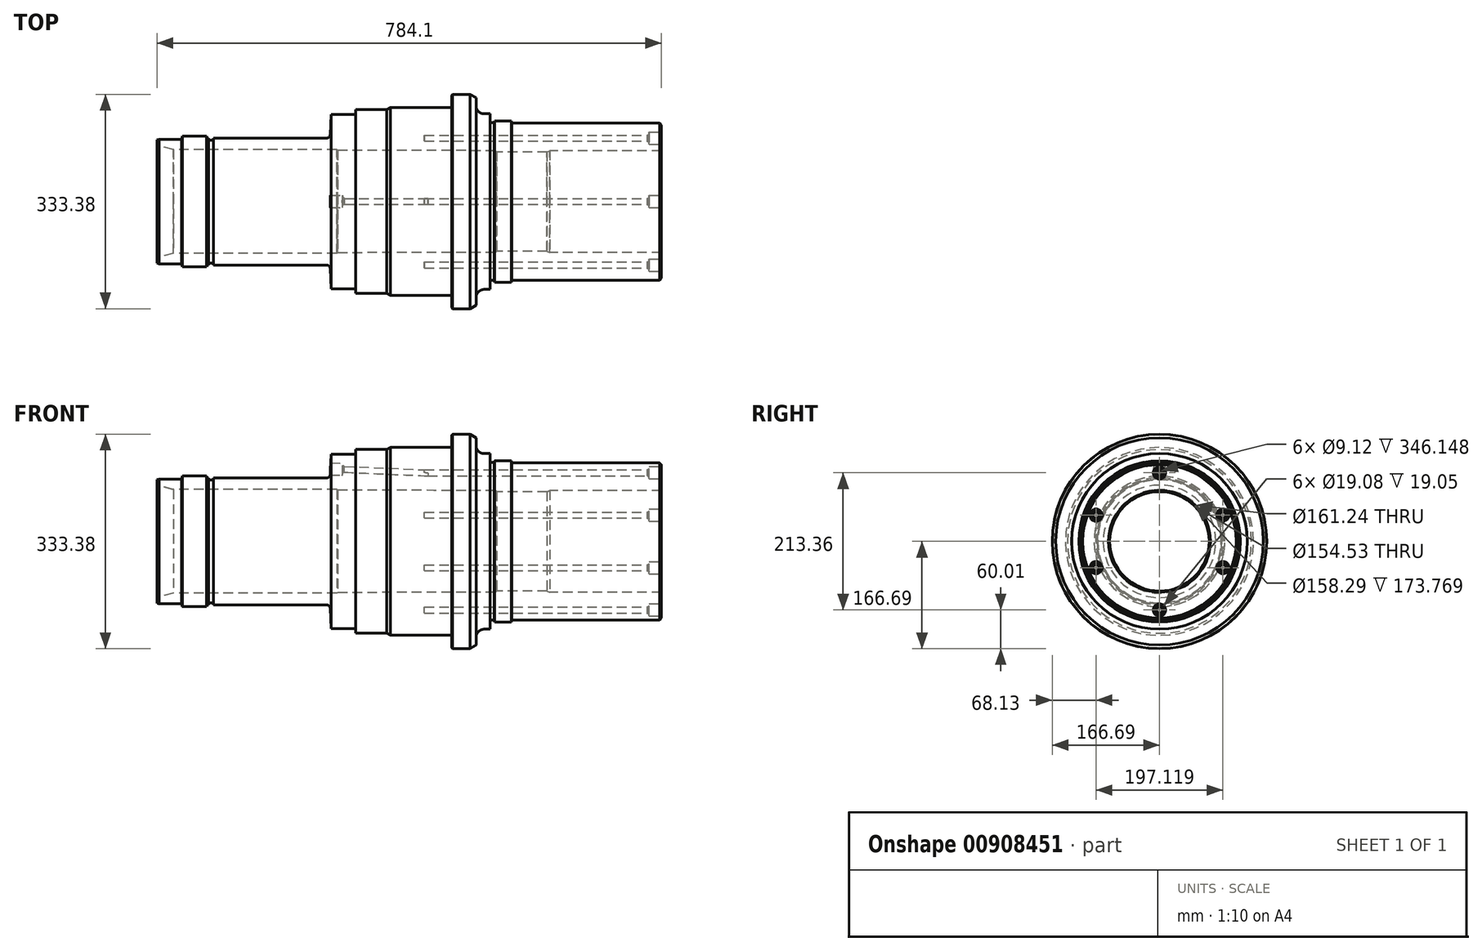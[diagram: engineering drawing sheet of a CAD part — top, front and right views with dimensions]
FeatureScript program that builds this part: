
annotation { "Feature Type Name" : "Feature", "Feature Type Description" : "" }
export const myFeature = defineFeature(function(context is Context, id is Id, definition is map)
    precondition{}
    {
        {
            var Q0;
            Q0=qCreatedBy(makeId("Front.planeOp"),FACE);
            var sketch = newSketch(context, id + "F0", { "sketchPlane" : qUnion([Q0])});
            skLineSegment(sketch, "E0", {"start": v(0, 0) * mm, "end": v(784.1, 0) * mm, "construction": true});
            skLineSegment(sketch, "E1", {"start": v(0, 96.84) * mm, "end": v(38.1, 96.84) * mm});
            skLineSegment(sketch, "E2", {"start": v(25.55, 80.62) * mm, "end": v(279.4, 80.62) * mm});
            skLineSegment(sketch, "E3", {"start": v(39.38, 101.6) * mm, "end": v(77, 101.6) * mm});
            skLineSegment(sketch, "E4", {"start": v(77.72, 98.87) * mm, "end": v(80.16, 98.87) * mm});
            skLineSegment(sketch, "E5", {"start": v(80.16, 98.87) * mm, "end": v(80.16, 95.7) * mm});
            skLineSegment(sketch, "E6", {"start": v(80.16, 95.7) * mm, "end": v(88.09, 95.7) * mm});
            skLineSegment(sketch, "E7", {"start": v(88.09, 95.7) * mm, "end": v(88.09, 98.87) * mm});
            skLineSegment(sketch, "E8", {"start": v(88.09, 98.87) * mm, "end": v(268.98, 98.87) * mm});
            skLineSegment(sketch, "E9", {"start": v(270.59, 135.64) * mm, "end": v(308.69, 135.64) * mm});
            skLineSegment(sketch, "E10", {"start": v(308.69, 135.64) * mm, "end": v(308.69, 142.88) * mm});
            skLineSegment(sketch, "E11", {"start": v(308.69, 142.88) * mm, "end": v(357.2, 142.88) * mm});
            skLineSegment(sketch, "E12", {"start": v(357.2, 142.87) * mm, "end": v(362.7, 146.05) * mm});
            skLineSegment(sketch, "E13", {"start": v(362.7, 146.05) * mm, "end": v(457.99, 146.05) * mm});
            skLineSegment(sketch, "E14", {"start": v(457.99, 146.05) * mm, "end": v(457.99, 166.69) * mm});
            skLineSegment(sketch, "E15", {"start": v(457.99, 166.69) * mm, "end": v(495.94, 166.69) * mm});
            skLineSegment(sketch, "E16", {"start": v(495.94, 166.69) * mm, "end": v(495.94, 136.53) * mm});
            skLineSegment(sketch, "E17", {"start": v(495.94, 136.53) * mm, "end": v(517.52, 136.53) * mm});
            skLineSegment(sketch, "E18", {"start": v(517.52, 136.53) * mm, "end": v(517.52, 122.5) * mm});
            skLineSegment(sketch, "E19", {"start": v(517.52, 122.5) * mm, "end": v(523.88, 122.5) * mm});
            skLineSegment(sketch, "E20", {"start": v(523.88, 122.5) * mm, "end": v(524.65, 125.41) * mm});
            skLineSegment(sketch, "E21", {"start": v(524.65, 125.41) * mm, "end": v(550.85, 125.41) * mm});
            skLineSegment(sketch, "E22", {"start": v(550.85, 125.41) * mm, "end": v(551.7, 122.24) * mm});
            skLineSegment(sketch, "E23", {"start": v(551.7, 122.24) * mm, "end": v(784.1, 122.24) * mm});
            skLineSegment(sketch, "E24", {"start": v(784.1, 79.15) * mm, "end": v(784.1, 122.24) * mm});
            skLineSegment(sketch, "E25", {"start": v(784.1, 79.15) * mm, "end": v(610.33, 79.15) * mm});
            skLineSegment(sketch, "E26", {"start": v(610.33, 79.15) * mm, "end": v(606.3, 77.27) * mm});
            skLineSegment(sketch, "E27", {"start": v(606.3, 77.27) * mm, "end": v(527.92, 77.27) * mm});
            skLineSegment(sketch, "E28", {"start": v(279.4, 80.62) * mm, "end": v(281.23, 79.57) * mm});
            skLineSegment(sketch, "E29", {"start": v(281.23, 79.57) * mm, "end": v(526.04, 79.15) * mm});
            skLineSegment(sketch, "E30", {"start": v(527.92, 77.27) * mm, "end": v(526.04, 79.15) * mm});
            skLineSegment(sketch, "E31", {"start": v(268.98, 98.87) * mm, "end": v(270.59, 135.64) * mm});
            skLineSegment(sketch, "E32", {"start": v(38.1, 96.84) * mm, "end": v(39.38, 101.6) * mm});
            skLineSegment(sketch, "E33", {"start": v(77.72, 98.87) * mm, "end": v(77, 101.6) * mm});
            skPoint(sketch, "E34.end.orphan", {"position": v(38.1, 101.6) * mm});
            skLineSegment(sketch, "E35", {"start": v(0, 87.46) * mm, "end": v(25.55, 80.62) * mm});
            skLineSegment(sketch, "E36", {"start": v(0, 96.84) * mm, "end": v(0, 87.46) * mm});
            skSolve(sketch);
        }
        {
            var Q0;
            Q0=qSketchRegion(id+"F0",true);
            var Q1;
            Q1=sQuery(id+"F0.wireOp",EDGE,"E0");
            revolve(context, id + "F1", {"surfaceOperationType" : NewSurfaceOperationType.NEW, "entities" : qUnion([Q0]), "axis" : qUnion([Q1]), "revolveType" : RevolveType.FULL});
        }
        {
            var Q0;
            Q0=makeQuery(id+"F1.opRevolve","SWEPT_EDGE",EDGE,{"disambiguationData":[OSD([sQuery(id+"F0.wireOp",EDGE,"E15"),sQuery(id+"F0.wireOp",EDGE,"E16")])]});
            chamfer(context, id + "F2", {"entities" : qUnion([Q0]), "chamferType" : ChamferType.OFFSET_ANGLE, "width" : 9.52 * mm, "oppositeDirection" : false, "angle" : 30 * degree, "tangentPropagation" : true});
        }
        {
            var Q0;
            Q0=makeQuery(id+"F1.opRevolve","SWEPT_EDGE",EDGE,{"disambiguationData":[OSD([sQuery(id+"F0.wireOp",EDGE,"E16"),sQuery(id+"F0.wireOp",EDGE,"E17")])]});
            fillet(context, id + "F3", {"entities" : qUnion([Q0]), "radius" : 12.7 * mm, "tangentPropagation" : true, "allowEdgeOverflow" : false});
        }
        {
            var Q0;
            Q0=makeQuery(id+"F1.opRevolve","SWEPT_EDGE",EDGE,{"disambiguationData":[OSD([sQuery(id+"F0.wireOp",EDGE,"E8"),sQuery(id+"F0.wireOp",EDGE,"E31")])]});
            fillet(context, id + "F4", {"entities" : qUnion([Q0]), "radius" : 5.08 * mm, "tangentPropagation" : true, "allowEdgeOverflow" : false});
        }
        {
            var Q0;
            Q0=makeQuery(id+"F1.opRevolve","SWEPT_EDGE",EDGE,{"disambiguationData":[OSD([sQuery(id+"F0.wireOp",EDGE,"E1"),sQuery(id+"F0.wireOp",EDGE,"SCYpA8kQ-7sTV-xUNJ-m1pp-K6qHX3d4gstn")])]});
            chamfer(context, id + "F5", {"entities" : qUnion([Q0]), "chamferType" : ChamferType.OFFSET_ANGLE, "width" : 0.86 * mm, "oppositeDirection" : false, "angle" : 75 * degree, "tangentPropagation" : true});
        }
        {
            var Q0;
            Q0=makeQuery(id+"F1.opRevolve","SWEPT_EDGE",EDGE,{"disambiguationData":[OSD([sQuery(id+"F0.wireOp",EDGE,"E23"),sQuery(id+"F0.wireOp",EDGE,"E24")])]});
            chamfer(context, id + "F6", {"entities" : qUnion([Q0]), "width" : 3.05 * mm, "tangentPropagation" : true});
        }
        {
            var Q0;
            Q0=makeQuery(id+"F1.opRevolve","SWEPT_EDGE",EDGE,{"disambiguationData":[OSD([sQuery(id+"F0.wireOp",EDGE,"E14"),sQuery(id+"F0.wireOp",EDGE,"E15")])]});
            chamfer(context, id + "F7", {"entities" : qUnion([Q0]), "width" : 1.52 * mm, "tangentPropagation" : true});
        }
        {
            var Q0;
            Q0=makeQuery(id+"F1.opRevolve","SWEPT_FACE",FACE,{"disambiguationData":[OSD([sQuery(id+"F0.wireOp",EDGE,"E24")])]});
            var sketch = newSketch(context, id + "F8", { "sketchPlane" : qUnion([Q0])});
            skCircle(sketch, "E37", {"center": v(0, 106.68) * mm, "radius": 4.56 * mm});
            skCircle(sketch, "E38", {"center": v(0, -106.68) * mm, "radius": 4.56 * mm});
            skCircle(sketch, "E39", {"center": v(98.52, 40.92) * mm, "radius": 4.56 * mm});
            skCircle(sketch, "E40", {"center": v(98.56, -40.82) * mm, "radius": 4.56 * mm});
            skCircle(sketch, "E41", {"center": v(-98.56, -40.82) * mm, "radius": 4.56 * mm});
            skCircle(sketch, "E42", {"center": v(-98.56, 40.83) * mm, "radius": 4.56 * mm});
            skLineSegment(sketch, "E43", {"start": v(-107.72, 0) * mm, "end": v(113.39, 0) * mm, "construction": true});
            skLineSegment(sketch, "E44", {"start": v(0, 0) * mm, "end": v(98.52, 40.92) * mm, "construction": true});
            skLineSegment(sketch, "E45", {"start": v(0, 0) * mm, "end": v(-98.56, 40.83) * mm, "construction": true});
            skLineSegment(sketch, "E46", {"start": v(0, 0) * mm, "end": v(-98.56, -40.82) * mm, "construction": true});
            skLineSegment(sketch, "E47", {"start": v(0, 0) * mm, "end": v(98.56, -40.82) * mm, "construction": true});
            skSolve(sketch);
        }
        {
            var Q0;
            Q0=qSketchRegion(id+"F8",true);
            extrude(context, id + "F9", {"entities" : qUnion([Q0]), "operationType" : NewBodyOperationType.REMOVE, "oppositeDirection" : true, "depth" : 368.3 * mm, "offsetDistance" : 25.4 * mm});
        }
        {
            var Q0;
            Q0=makeQuery(id+"F1.opRevolve","SWEPT_FACE",FACE,{"disambiguationData":[OSD([sQuery(id+"F0.wireOp",EDGE,"E24")])]});
            var sketch = newSketch(context, id + "F10", { "sketchPlane" : qUnion([Q0])});
            skCircle(sketch, "E48", {"center": v(98.52, 40.92) * mm, "radius": 9.54 * mm});
            skCircle(sketch, "E49", {"center": v(0, 106.68) * mm, "radius": 9.54 * mm});
            skCircle(sketch, "E50", {"center": v(-98.56, 40.83) * mm, "radius": 9.54 * mm});
            skCircle(sketch, "E51", {"center": v(-98.56, -40.82) * mm, "radius": 9.54 * mm});
            skCircle(sketch, "E52", {"center": v(98.56, -40.82) * mm, "radius": 9.54 * mm});
            skCircle(sketch, "E53", {"center": v(0, -106.68) * mm, "radius": 9.54 * mm});
            skSolve(sketch);
        }
        {
            var Q0;
            Q0=qSketchRegion(id+"F10",true);
            extrude(context, id + "F11", {"entities" : qUnion([Q0]), "operationType" : NewBodyOperationType.REMOVE, "oppositeDirection" : true, "depth" : 19.05 * mm, "offsetDistance" : 25.4 * mm});
        }
        {
            var Q0;
            Q0=makeQuery(id+"F11.boolean.opBoolean","INTERSECT",EDGE,{"derivedFrom":[makeQuery(id+"F9.boolean.opBoolean","COPY",FACE,{"derivedFrom":makeQuery(id+"F9.opExtrude","SWEPT_FACE",FACE,{"disambiguationData":[OSD([sQuery(id+"F8.wireOp",EDGE,"E37")])]})}),makeQuery(id+"F11.opExtrude","CAP_FACE",FACE,{"disambiguationData":[OSD([sQuery(id+"F10.wireOp",EDGE,"E49")])],"isStart":false})]});
            var Q1;
            Q1=makeQuery(id+"F11.boolean.opBoolean","INTERSECT",EDGE,{"derivedFrom":[makeQuery(id+"F9.boolean.opBoolean","COPY",FACE,{"derivedFrom":makeQuery(id+"F9.opExtrude","SWEPT_FACE",FACE,{"disambiguationData":[OSD([sQuery(id+"F8.wireOp",EDGE,"E42")])]})}),makeQuery(id+"F11.opExtrude","CAP_FACE",FACE,{"disambiguationData":[OSD([sQuery(id+"F10.wireOp",EDGE,"E50")])],"isStart":false})]});
            var Q2;
            Q2=makeQuery(id+"F11.boolean.opBoolean","INTERSECT",EDGE,{"derivedFrom":[makeQuery(id+"F9.boolean.opBoolean","COPY",FACE,{"derivedFrom":makeQuery(id+"F9.opExtrude","SWEPT_FACE",FACE,{"disambiguationData":[OSD([sQuery(id+"F8.wireOp",EDGE,"E38")])]})}),makeQuery(id+"F11.opExtrude","CAP_FACE",FACE,{"disambiguationData":[OSD([sQuery(id+"F10.wireOp",EDGE,"E53")])],"isStart":false})]});
            var Q3;
            Q3=makeQuery(id+"F11.boolean.opBoolean","INTERSECT",EDGE,{"derivedFrom":[makeQuery(id+"F9.boolean.opBoolean","COPY",FACE,{"derivedFrom":makeQuery(id+"F9.opExtrude","SWEPT_FACE",FACE,{"disambiguationData":[OSD([sQuery(id+"F8.wireOp",EDGE,"E41")])]})}),makeQuery(id+"F11.opExtrude","CAP_FACE",FACE,{"disambiguationData":[OSD([sQuery(id+"F10.wireOp",EDGE,"E51")])],"isStart":false})]});
            var Q4;
            Q4=makeQuery(id+"F11.boolean.opBoolean","INTERSECT",EDGE,{"derivedFrom":[makeQuery(id+"F9.boolean.opBoolean","COPY",FACE,{"derivedFrom":makeQuery(id+"F9.opExtrude","SWEPT_FACE",FACE,{"disambiguationData":[OSD([sQuery(id+"F8.wireOp",EDGE,"E40")])]})}),makeQuery(id+"F11.opExtrude","CAP_FACE",FACE,{"disambiguationData":[OSD([sQuery(id+"F10.wireOp",EDGE,"E52")])],"isStart":false})]});
            var Q5;
            Q5=makeQuery(id+"F11.boolean.opBoolean","INTERSECT",EDGE,{"derivedFrom":[makeQuery(id+"F9.boolean.opBoolean","COPY",FACE,{"derivedFrom":makeQuery(id+"F9.opExtrude","SWEPT_FACE",FACE,{"disambiguationData":[OSD([sQuery(id+"F8.wireOp",EDGE,"E39")])]})}),makeQuery(id+"F11.opExtrude","CAP_FACE",FACE,{"disambiguationData":[OSD([sQuery(id+"F10.wireOp",EDGE,"E48")])],"isStart":false})]});
            chamfer(context, id + "F12", {"entities" : qUnion([Q0, Q1, Q2, Q3, Q4, Q5]), "chamferType" : ChamferType.OFFSET_ANGLE, "width" : 1.8 * mm, "oppositeDirection" : false, "angle" : 60 * degree, "tangentPropagation" : true});
        }
        {
            var Q0;
            Q0=qCreatedBy(makeId("Front.planeOp"),FACE);
            var sketch = newSketch(context, id + "F13", { "sketchPlane" : qUnion([Q0])});
            skPoint(sketch, "E54", {"position": v(270.59, 135.64) * mm});
            skPoint(sketch, "E55", {"position": v(269.6, 113.03) * mm});
            skLineSegment(sketch, "E56", {"start": v(269.6, 113.03) * mm, "end": v(422.8, 106.34) * mm});
            skLineSegment(sketch, "E57.0", {"start": v(269.19, 103.58) * mm, "end": v(288.22, 102.75) * mm});
            skPoint(sketch, "E58", {"position": v(288.63, 112.2) * mm});
            skPoint(sketch, "E59", {"position": v(310.92, 59.6) * mm});
            skPoint(sketch, "E60", {"position": v(288.35, 105.86) * mm});
            skLineSegment(sketch, "E61", {"start": v(288.35, 105.86) * mm, "end": v(290.97, 107.53) * mm});
            skLineSegment(sketch, "E62.trimOffspring", {"start": v(290.97, 107.53) * mm, "end": v(421, 101.86) * mm});
            skLineSegment(sketch, "E63", {"start": v(269.19, 103.58) * mm, "end": v(264.76, 103.58) * mm});
            skLineSegment(sketch, "E64", {"start": v(264.76, 103.58) * mm, "end": v(264.76, 110.78) * mm});
            skLineSegment(sketch, "E65.trimOffspring", {"start": v(288.35, 105.86) * mm, "end": v(288.22, 102.75) * mm});
            skLineSegment(sketch, "E66", {"start": v(269.6, 113.03) * mm, "end": v(264.76, 110.78) * mm});
            skLineSegment(sketch, "E67", {"start": v(422.8, 106.34) * mm, "end": v(421, 101.86) * mm});
            skSolve(sketch);
        }
        {
            var Q0;
            Q0 = qSketchRegion(id + "F13", true);
            var Q1;
            Q1=sQuery(id+"F13.wireOp",EDGE,"E56");
            revolve(context, id + "F14", {"operationType" : NewBodyOperationType.REMOVE, "surfaceOperationType" : NewSurfaceOperationType.NEW, "entities" : qUnion([Q0]), "axis" : qUnion([Q1]), "revolveType" : RevolveType.FULL, "oppositeDirection" : true});
        }
    });
